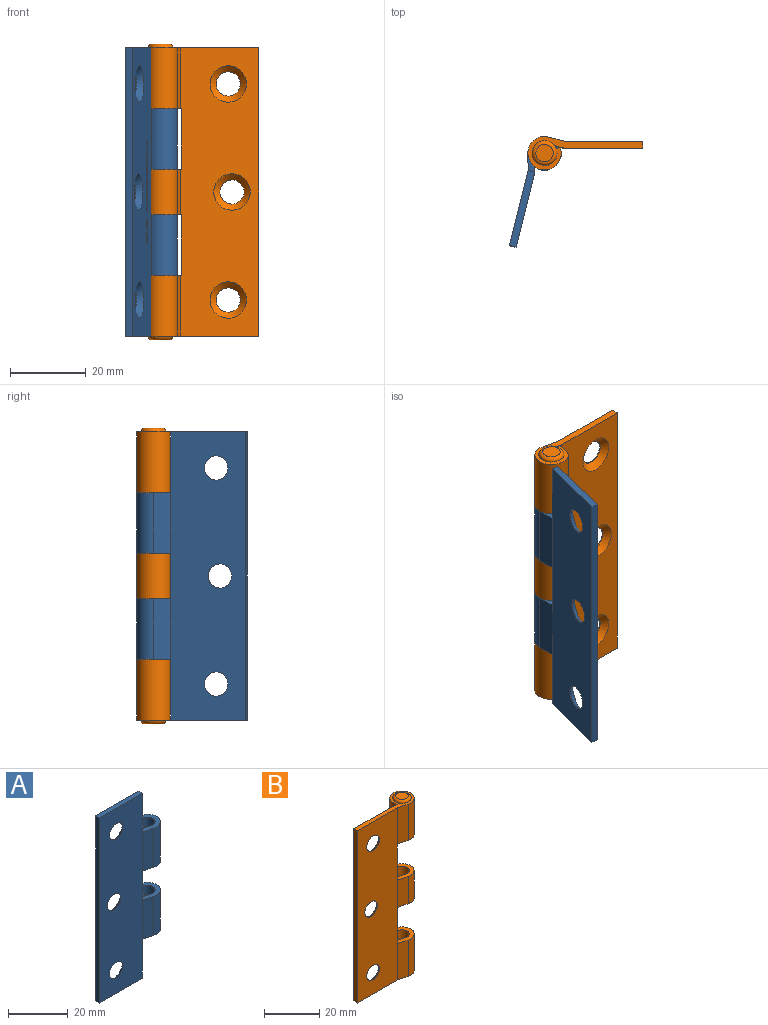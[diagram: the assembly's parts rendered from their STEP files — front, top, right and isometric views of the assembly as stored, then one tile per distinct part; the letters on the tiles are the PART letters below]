
ASSEMBLY  parts=2 mates=1
PART A: 283 faces, bbox 30.3x8.8x76 mm
  f0: cone r=3.2mm half-angle=45deg, axis (0,1,0), area 56.9mm2, adj f3,f10
  f1: cone r=3.2mm half-angle=45deg, axis (0,1,0), area 56.9mm2, adj f4,f10
  f2: cone r=3.2mm half-angle=45deg, axis (0,1,0), area 56.9mm2, adj f5,f10
  f3: cylinder r=3.2mm len=6.4mm, axis (0,1,0), area 4mm2, adj f0,f16
  f4: cylinder r=3.2mm len=6.4mm, axis (0,1,0), area 4mm2, adj f1,f16
  f5: cylinder r=3.2mm len=6.4mm, axis (0,1,0), area 4mm2, adj f2,f16
  f6: cylinder r=4.4mm len=16mm, axis (0,0,-1), area 374.3mm2, adj f17,f18,f23,f24
  f7: cylinder r=2.6mm len=16mm, axis (0,0,-1), area 221.2mm2, adj f14,f18,f23,f24
  f8: cylinder r=4.4mm len=16mm, axis (0,0,-1), area 374.3mm2, adj f12,f13,f22,f26
  f9: cylinder r=2.6mm len=16mm, axis (0,0,-1), area 221.2mm2, adj f11,f13,f22,f26
  f10: plane 76x20.64mm, normal (0,1,0), area 1324.3mm2, adj f0,f1,f2,f11,f14,f15,f19,f20
  f11: plane 16x4.54mm, normal (0.26,0.97,0), area 75.2mm2, adj f9,f10,f22,f26
  f12: plane 16x4.32mm, normal (-0.26,-0.97,0), area 71.5mm2, adj f8,f16,f22,f26
  f13: plane 16x1.69mm, normal (0.34,-0.94,0), area 28.8mm2, adj f8,f9,f22,f26
  f14: plane 16x4.54mm, normal (0.26,0.97,0), area 75.2mm2, adj f7,f10,f23,f24
  f15: plane 76x1.8mm, normal (-1,0,0), area 136.8mm2, adj f10,f16,f19,f20
  f16: plane 76x20.4mm, normal (0,-1,0), area 1453.9mm2, adj f3,f4,f5,f12,f15,f17,f19,f20
  f17: plane 16x4.32mm, normal (-0.26,-0.97,0), area 71.5mm2, adj f6,f16,f23,f24
  f18: plane 16x1.69mm, normal (0.34,-0.94,0), area 28.8mm2, adj f6,f7,f23,f24
  f19: plane 20.4x1.8mm, normal (0,0,1), area 36.7mm2, adj f10,f15,f16,f27
  f20: plane 20.4x1.8mm, normal (0,0,-1), area 36.7mm2, adj f10,f15,f16,f25
  f21: plane 12x1.8mm, normal (1,0,0), area 21.6mm2, adj f10,f16,f22,f23
  f22: plane 9.85x8.8mm, normal (0,0,-1), area 42mm2, adj f8,f9,f10,f11,f12,f13,f21
  f23: plane 9.85x8.8mm, normal (0,0,1), area 42mm2, adj f6,f7,f10,f14,f17,f18,f21
  f24: plane 9.85x8.8mm, normal (0,0,-1), area 42mm2, adj f6,f7,f10,f14,f17,f18,f25
  f25: plane 16x1.8mm, normal (1,0,0), area 28.8mm2, adj f10,f16,f20,f24
  f26: plane 9.85x8.8mm, normal (0,0,1), area 42mm2, adj f8,f9,f10,f11,f12,f13,f27
  f27: plane 16x1.8mm, normal (1,0,0), area 28.8mm2, adj f10,f16,f19,f26
  f28: plane 0.25x0.23mm, normal (1,0,0), area 0.1mm2, adj f10,f29,f45,f46
  f29: plane 1.45x0.37mm, normal (0.24,0,0.97), area 0.4mm2, adj f10,f28,f30,f46
  f30: plane 0.25x0.21mm, normal (-1,0,0), area 0.1mm2, adj f10,f29,f31,f46
  f31: plane 0.83x0.25mm, normal (-0.23,0,-0.97), area 0.2mm2, adj f10,f30,f32,f46
  f32: plane 0.31x0.25mm, normal (-0.23,0,-0.97), area 0.1mm2, adj f10,f31,f33,f46
  f33: plane 0.3x0.25mm, normal (-0.19,0,0.98), area 0.1mm2, adj f10,f32,f34,f46
  f34: plane 0.85x0.25mm, normal (-0.19,0,0.98), area 0.2mm2, adj f10,f33,f35,f46
  f35: plane 0.25x0.23mm, normal (-1,0,0), area 0.1mm2, adj f10,f34,f36,f46
  f36: plane 0.84x0.25mm, normal (-0.19,0,-0.98), area 0.2mm2, adj f10,f35,f37,f46
  f37: plane 0.28x0.25mm, normal (-0.2,0,-0.98), area 0.1mm2, adj f10,f36,f38,f46
  f38: plane 0.28x0.25mm, normal (-0.23,0,0.97), area 0.1mm2, adj f10,f37,f39,f46
  f39: plane 0.84x0.25mm, normal (-0.23,0,0.97), area 0.2mm2, adj f10,f38,f40,f46
  f40: plane 0.25x0.21mm, normal (-1,0,0), area 0.1mm2, adj f10,f39,f41,f46
  f41: plane 1.45x0.35mm, normal (0.23,0,-0.97), area 0.4mm2, adj f10,f40,f42,f46
  f42: plane 0.25x0.25mm, normal (1,0,0), area 0.1mm2, adj f10,f41,f43,f46
  f43: plane 0.87x0.25mm, normal (0.2,0,0.98), area 0.2mm2, adj f10,f42,f44,f46
  f44: plane 0.25x0.25mm, normal (0.17,0,0.99), area 0.1mm2, adj f10,f43,f45,f46
  f45: plane 1.12x0.25mm, normal (0.19,0,-0.98), area 0.3mm2, adj f10,f28,f44,f46
  f46: plane 1.64x1.45mm, normal (0,1,0), area 1.1mm2, adj f28,f29,f30,f31,f32,f33,f34,f35
  f47: plane 0.25x0.23mm, normal (1,0,0), area 0.1mm2, adj f10,f48,f64,f65
  f48: plane 1.45x0.37mm, normal (0.24,0,0.97), area 0.4mm2, adj f10,f47,f49,f65
  f49: plane 0.25x0.21mm, normal (-1,0,0), area 0.1mm2, adj f10,f48,f50,f65
  f50: plane 0.83x0.25mm, normal (-0.23,0,-0.97), area 0.2mm2, adj f10,f49,f51,f65
  f51: plane 0.31x0.25mm, normal (-0.23,0,-0.97), area 0.1mm2, adj f10,f50,f52,f65
  f52: plane 0.3x0.25mm, normal (-0.19,0,0.98), area 0.1mm2, adj f10,f51,f53,f65
  f53: plane 0.85x0.25mm, normal (-0.19,0,0.98), area 0.2mm2, adj f10,f52,f54,f65
  f54: plane 0.25x0.23mm, normal (-1,0,0), area 0.1mm2, adj f10,f53,f55,f65
  f55: plane 0.84x0.25mm, normal (-0.19,0,-0.98), area 0.2mm2, adj f10,f54,f56,f65
  f56: plane 0.28x0.25mm, normal (-0.2,0,-0.98), area 0.1mm2, adj f10,f55,f57,f65
  f57: plane 0.28x0.25mm, normal (-0.23,0,0.97), area 0.1mm2, adj f10,f56,f58,f65
  f58: plane 0.84x0.25mm, normal (-0.23,0,0.97), area 0.2mm2, adj f10,f57,f59,f65
  f59: plane 0.25x0.21mm, normal (-1,0,0), area 0.1mm2, adj f10,f58,f60,f65
  f60: plane 1.45x0.35mm, normal (0.23,0,-0.97), area 0.4mm2, adj f10,f59,f61,f65
  f61: plane 0.25x0.25mm, normal (1,0,0), area 0.1mm2, adj f10,f60,f62,f65
  f62: plane 0.87x0.25mm, normal (0.2,0,0.98), area 0.2mm2, adj f10,f61,f63,f65
  f63: plane 0.25x0.25mm, normal (0.17,0,0.99), area 0.1mm2, adj f10,f62,f64,f65
  f64: plane 1.12x0.25mm, normal (0.19,0,-0.98), area 0.3mm2, adj f10,f47,f63,f65
  f65: plane 1.64x1.45mm, normal (0,1,0), area 1.1mm2, adj f47,f48,f49,f50,f51,f52,f53,f54
  f66: plane 0.25x0.23mm, normal (1,0,0), area 0.1mm2, adj f10,f67,f83,f84
  f67: plane 1.45x0.37mm, normal (0.24,0,0.97), area 0.4mm2, adj f10,f66,f68,f84
  f68: plane 0.25x0.21mm, normal (-1,0,0), area 0.1mm2, adj f10,f67,f69,f84
  f69: plane 0.83x0.25mm, normal (-0.23,0,-0.97), area 0.2mm2, adj f10,f68,f70,f84
  f70: plane 0.31x0.25mm, normal (-0.23,0,-0.97), area 0.1mm2, adj f10,f69,f71,f84
  f71: plane 0.3x0.25mm, normal (-0.19,0,0.98), area 0.1mm2, adj f10,f70,f72,f84
  f72: plane 0.85x0.25mm, normal (-0.19,0,0.98), area 0.2mm2, adj f10,f71,f73,f84
  f73: plane 0.25x0.23mm, normal (-1,0,0), area 0.1mm2, adj f10,f72,f74,f84
  f74: plane 0.84x0.25mm, normal (-0.19,0,-0.98), area 0.2mm2, adj f10,f73,f75,f84
  f75: plane 0.28x0.25mm, normal (-0.2,0,-0.98), area 0.1mm2, adj f10,f74,f76,f84
  f76: plane 0.28x0.25mm, normal (-0.23,0,0.97), area 0.1mm2, adj f10,f75,f77,f84
  f77: plane 0.84x0.25mm, normal (-0.23,0,0.97), area 0.2mm2, adj f10,f76,f78,f84
  f78: plane 0.25x0.21mm, normal (-1,0,0), area 0.1mm2, adj f10,f77,f79,f84
  f79: plane 1.45x0.35mm, normal (0.23,0,-0.97), area 0.4mm2, adj f10,f78,f80,f84
  f80: plane 0.25x0.25mm, normal (1,0,0), area 0.1mm2, adj f10,f79,f81,f84
  f81: plane 0.87x0.25mm, normal (0.2,0,0.98), area 0.2mm2, adj f10,f80,f82,f84
  f82: plane 0.25x0.25mm, normal (0.17,0,0.99), area 0.1mm2, adj f10,f81,f83,f84
  f83: plane 1.12x0.25mm, normal (0.19,0,-0.98), area 0.3mm2, adj f10,f66,f82,f84
  f84: plane 1.64x1.45mm, normal (0,1,0), area 1.1mm2, adj f66,f67,f68,f69,f70,f71,f72,f73
  f85: plane 0.25x0.21mm, normal (1,0,0), area 0.1mm2, adj f10,f86,f88,f89
  f86: plane 0.29x0.25mm, normal (0,0,1), area 0.1mm2, adj f10,f85,f87,f89
  f87: plane 0.25x0.21mm, normal (-1,0,0), area 0.1mm2, adj f10,f86,f88,f89
  f88: plane 0.29x0.25mm, normal (0,0,-1), area 0.1mm2, adj f10,f85,f87,f89
  f89: plane 0.29x0.21mm, normal (0,1,0), area 0.1mm2, adj f85,f86,f87,f88
  f90: extruded ~0.36x0.3mm, area 0.1mm2, adj f10,f91,f99,f100
  f91: plane 0.25x0.21mm, normal (-0.99,0,-0.12), area 0.1mm2, adj f10,f90,f92,f100
  f92: extruded ~0.55x0.5mm, area 0.2mm2, adj f10,f91,f93,f100
  f93: extruded ~0.75x0.54mm, area 0.3mm2, adj f10,f92,f94,f100
  f94: extruded ~0.75x0.54mm, area 0.3mm2, adj f10,f93,f95,f100
  f95: extruded ~0.47x0.47mm, area 0.2mm2, adj f10,f94,f96,f100
  f96: plane 0.25x0.21mm, normal (0.99,0,-0.12), area 0.1mm2, adj f10,f95,f97,f100
  f97: extruded ~0.29x0.26mm, area 0.1mm2, adj f10,f96,f98,f100
  f98: extruded ~0.54x0.33mm, area 0.2mm2, adj f10,f97,f99,f100
  f99: extruded ~0.55x0.33mm, area 0.2mm2, adj f10,f90,f98,f100
  f100: plane 1.51x1.04mm, normal (0,1,0), area 0.6mm2, adj f90,f91,f92,f93,f94,f95,f96,f97
  f101: extruded ~0.75x0.56mm, area 0.3mm2, adj f10,f102,f104,f105
  f102: extruded ~0.75x0.56mm, area 0.3mm2, adj f10,f101,f103,f105
  f103: extruded ~0.74x0.56mm, area 0.3mm2, adj f10,f102,f104,f105
  f104: extruded ~0.77x0.56mm, area 0.3mm2, adj f10,f101,f103,f105
  f105: plane 1.51x1.12mm, normal (0,1,0), area 0.7mm2, adj f101,f102,f103,f104,f106,f107,f108,f109
  f106: extruded ~0.54x0.35mm, area 0.2mm2, adj f105,f107,f109,f110
  f107: extruded ~0.54x0.36mm, area 0.2mm2, adj f105,f106,f108,f110
  f108: extruded ~0.55x0.35mm, area 0.2mm2, adj f105,f107,f109,f110
  f109: extruded ~0.55x0.36mm, area 0.2mm2, adj f105,f106,f108,f110
  f110: plane 1.09x0.7mm, normal (0,1,0), area 0.6mm2, adj f106,f107,f108,f109
  f111: plane 0.25x0.21mm, normal (1,0,0), area 0.1mm2, adj f10,f112,f129,f130
  f112: plane 1.45x0.25mm, normal (0,0,1), area 0.4mm2, adj f10,f111,f113,f130
  f113: plane 0.25x0.18mm, normal (-1,0,0), area 0mm2, adj f10,f112,f114,f130
  f114: plane 0.25x0.21mm, normal (0,0,-1), area 0.1mm2, adj f10,f113,f115,f130
  f115: extruded ~0.36x0.25mm, area 0.1mm2, adj f10,f114,f116,f130
  f116: extruded ~0.34x0.25mm, area 0.1mm2, adj f10,f115,f117,f130
  f117: extruded ~0.37x0.25mm, area 0.1mm2, adj f10,f116,f118,f130
  f118: extruded ~0.49x0.37mm, area 0.2mm2, adj f10,f117,f119,f130
  f119: plane 0.99x0.25mm, normal (0,0,-1), area 0.2mm2, adj f10,f118,f120,f130
  f120: plane 0.25x0.21mm, normal (1,0,0), area 0.1mm2, adj f10,f119,f121,f130
  f121: plane 0.92x0.25mm, normal (0,0,1), area 0.2mm2, adj f10,f120,f122,f130
  f122: extruded ~0.36x0.25mm, area 0.1mm2, adj f10,f121,f123,f130
  f123: extruded ~0.43x0.29mm, area 0.1mm2, adj f10,f122,f124,f130
  f124: plane 0.84x0.25mm, normal (0,0,-1), area 0.2mm2, adj f10,f123,f125,f130
  f125: plane 0.25x0.21mm, normal (1,0,0), area 0.1mm2, adj f10,f124,f126,f130
  f126: plane 0.94x0.25mm, normal (0,0,1), area 0.2mm2, adj f10,f125,f127,f130
  f127: extruded ~0.33x0.25mm, area 0.1mm2, adj f10,f126,f128,f130
  f128: extruded ~0.52x0.29mm, area 0.2mm2, adj f10,f127,f129,f130
  f129: plane 0.75x0.25mm, normal (0,0,-1), area 0.2mm2, adj f10,f111,f128,f130
  f130: plane 1.61x1.48mm, normal (0,1,0), area 1.1mm2, adj f111,f112,f113,f114,f115,f116,f117,f118
  f131: extruded ~0.25x0.2mm, area 0.1mm2, adj f10,f132,f145,f146
  f132: extruded ~0.44x0.25mm, area 0.1mm2, adj f10,f131,f133,f146
  f133: extruded ~0.41x0.41mm, area 0.2mm2, adj f10,f132,f134,f146
  f134: extruded ~0.48x0.45mm, area 0.2mm2, adj f10,f133,f135,f146
  f135: extruded ~0.37x0.25mm, area 0.1mm2, adj f10,f134,f136,f146
  f136: plane 0.25x0.06mm, normal (0,0,1), area 0mm2, adj f10,f135,f137,f146
  f137: extruded ~0.25x0.2mm, area 0.1mm2, adj f10,f136,f138,f146
  f138: extruded ~0.25x0.24mm, area 0.1mm2, adj f10,f137,f139,f146
  f139: extruded ~0.33x0.26mm, area 0.1mm2, adj f10,f138,f140,f146
  f140: plane 0.25x0.21mm, normal (0.99,0,0.12), area 0.1mm2, adj f10,f139,f141,f146
  f141: extruded ~0.56x0.44mm, area 0.2mm2, adj f10,f140,f142,f146
  f142: extruded ~0.55x0.48mm, area 0.2mm2, adj f10,f141,f143,f146
  f143: plane 0.33x0.25mm, normal (0,0,-1), area 0.1mm2, adj f10,f142,f144,f146
  f144: extruded ~0.61x0.25mm, area 0.2mm2, adj f10,f143,f145,f146
  f145: plane 0.25x0.21mm, normal (1,0,0), area 0.1mm2, adj f10,f131,f144,f146
  f146: plane 1.51x1.12mm, normal (0,1,0), area 0.9mm2, adj f131,f132,f133,f134,f135,f136,f137,f138
  f147: plane 0.25x0.09mm, normal (0,0,1), area 0mm2, adj f146,f148,f151,f152
  f148: extruded ~0.46x0.39mm, area 0.2mm2, adj f146,f147,f149,f152
  f149: extruded ~0.26x0.25mm, area 0.1mm2, adj f146,f148,f150,f152
  f150: extruded ~0.3x0.25mm, area 0.1mm2, adj f146,f149,f151,f152
  f151: extruded ~0.35x0.25mm, area 0.1mm2, adj f146,f147,f150,f152
  f152: plane 0.65x0.55mm, normal (0,1,0), area 0.2mm2, adj f147,f148,f149,f150,f151
  f153: extruded ~0.36x0.3mm, area 0.1mm2, adj f10,f154,f162,f163
  f154: plane 0.25x0.21mm, normal (-0.99,0,-0.12), area 0.1mm2, adj f10,f153,f155,f163
  f155: extruded ~0.55x0.5mm, area 0.2mm2, adj f10,f154,f156,f163
  f156: extruded ~0.75x0.54mm, area 0.3mm2, adj f10,f155,f157,f163
  f157: extruded ~0.75x0.54mm, area 0.3mm2, adj f10,f156,f158,f163
  f158: extruded ~0.47x0.47mm, area 0.2mm2, adj f10,f157,f159,f163
  f159: plane 0.25x0.21mm, normal (0.99,0,-0.12), area 0.1mm2, adj f10,f158,f160,f163
  f160: extruded ~0.29x0.26mm, area 0.1mm2, adj f10,f159,f161,f163
  f161: extruded ~0.54x0.33mm, area 0.2mm2, adj f10,f160,f162,f163
  f162: extruded ~0.55x0.33mm, area 0.2mm2, adj f10,f153,f161,f163
  f163: plane 1.51x1.04mm, normal (0,1,0), area 0.6mm2, adj f153,f154,f155,f156,f157,f158,f159,f160
  f164: plane 0.25x0.21mm, normal (1,0,0), area 0.1mm2, adj f10,f165,f167,f168
  f165: plane 0.29x0.25mm, normal (0,0,1), area 0.1mm2, adj f10,f164,f166,f168
  f166: plane 0.25x0.21mm, normal (-1,0,0), area 0.1mm2, adj f10,f165,f167,f168
  f167: plane 0.29x0.25mm, normal (0,0,-1), area 0.1mm2, adj f10,f164,f166,f168
  f168: plane 0.29x0.21mm, normal (0,1,0), area 0.1mm2, adj f164,f165,f166,f167
  f169: extruded ~0.36x0.3mm, area 0.1mm2, adj f10,f170,f178,f179
  f170: plane 0.25x0.21mm, normal (-0.99,0,-0.12), area 0.1mm2, adj f10,f169,f171,f179
  f171: extruded ~0.55x0.5mm, area 0.2mm2, adj f10,f170,f172,f179
  f172: extruded ~0.75x0.54mm, area 0.3mm2, adj f10,f171,f173,f179
  f173: extruded ~0.75x0.54mm, area 0.3mm2, adj f10,f172,f174,f179
  f174: extruded ~0.47x0.47mm, area 0.2mm2, adj f10,f173,f175,f179
  f175: plane 0.25x0.21mm, normal (0.99,0,-0.12), area 0.1mm2, adj f10,f174,f176,f179
  f176: extruded ~0.29x0.26mm, area 0.1mm2, adj f10,f175,f177,f179
  f177: extruded ~0.54x0.33mm, area 0.2mm2, adj f10,f176,f178,f179
  f178: extruded ~0.55x0.33mm, area 0.2mm2, adj f10,f169,f177,f179
  f179: plane 1.51x1.04mm, normal (0,1,0), area 0.6mm2, adj f169,f170,f171,f172,f173,f174,f175,f176
  f180: extruded ~0.75x0.56mm, area 0.3mm2, adj f10,f181,f183,f184
  f181: extruded ~0.75x0.56mm, area 0.3mm2, adj f10,f180,f182,f184
  f182: extruded ~0.74x0.56mm, area 0.3mm2, adj f10,f181,f183,f184
  f183: extruded ~0.77x0.56mm, area 0.3mm2, adj f10,f180,f182,f184
  f184: plane 1.51x1.12mm, normal (0,1,0), area 0.7mm2, adj f180,f181,f182,f183,f185,f186,f187,f188
  f185: extruded ~0.54x0.35mm, area 0.2mm2, adj f184,f186,f188,f189
  f186: extruded ~0.54x0.36mm, area 0.2mm2, adj f184,f185,f187,f189
  f187: extruded ~0.55x0.35mm, area 0.2mm2, adj f184,f186,f188,f189
  f188: extruded ~0.55x0.36mm, area 0.2mm2, adj f184,f185,f187,f189
  f189: plane 1.09x0.7mm, normal (0,1,0), area 0.6mm2, adj f185,f186,f187,f188
  f190: plane 0.25x0.21mm, normal (1,0,0), area 0.1mm2, adj f10,f191,f193,f194
  f191: plane 0.29x0.25mm, normal (0,0,1), area 0.1mm2, adj f10,f190,f192,f194
  f192: plane 0.25x0.21mm, normal (-1,0,0), area 0.1mm2, adj f10,f191,f193,f194
  f193: plane 0.29x0.25mm, normal (0,0,-1), area 0.1mm2, adj f10,f190,f192,f194
  f194: plane 0.29x0.21mm, normal (0,1,0), area 0.1mm2, adj f190,f191,f192,f193
  f195: plane 0.25x0.21mm, normal (1,0,0), area 0.1mm2, adj f10,f196,f206,f207
  f196: plane 1.45x0.25mm, normal (0,0,1), area 0.4mm2, adj f10,f195,f197,f207
  f197: plane 0.25x0.18mm, normal (-1,0,0), area 0mm2, adj f10,f196,f198,f207
  f198: plane 0.25x0.21mm, normal (0,0,-1), area 0.1mm2, adj f10,f197,f199,f207
  f199: extruded ~0.38x0.25mm, area 0.1mm2, adj f10,f198,f200,f207
  f200: extruded ~0.59x0.4mm, area 0.2mm2, adj f10,f199,f201,f207
  f201: plane 0.89x0.25mm, normal (0,0,-1), area 0.2mm2, adj f10,f200,f202,f207
  f202: plane 0.25x0.21mm, normal (1,0,0), area 0.1mm2, adj f10,f201,f203,f207
  f203: plane 0.88x0.25mm, normal (0,0,1), area 0.2mm2, adj f10,f202,f204,f207
  f204: extruded ~0.39x0.25mm, area 0.1mm2, adj f10,f203,f205,f207
  f205: extruded ~0.48x0.31mm, area 0.2mm2, adj f10,f204,f206,f207
  f206: plane 0.79x0.25mm, normal (0,0,-1), area 0.2mm2, adj f10,f195,f205,f207
  f207: plane 1.48x0.96mm, normal (0,1,0), area 0.7mm2, adj f195,f196,f197,f198,f199,f200,f201,f202
  f208: plane 1.04x0.25mm, normal (1,0,0), area 0.3mm2, adj f10,f209,f218,f219
  f209: plane 0.25x0.21mm, normal (0,0,1), area 0.1mm2, adj f10,f208,f210,f219
  f210: plane 1.04x0.74mm, normal (-0.58,0,0.81), area 0.3mm2, adj f10,f209,f211,f219
  f211: plane 0.72x0.25mm, normal (1,0,0), area 0.2mm2, adj f10,f210,f212,f219
  f212: plane 0.25x0.21mm, normal (0,0,1), area 0.1mm2, adj f10,f211,f213,f219
  f213: plane 0.99x0.25mm, normal (-1,0,0), area 0.2mm2, adj f10,f212,f214,f219
  f214: plane 0.25x0.18mm, normal (0,0,-1), area 0mm2, adj f10,f213,f215,f219
  f215: plane 0.91x0.64mm, normal (0.58,0,-0.82), area 0.3mm2, adj f10,f214,f216,f219
  f216: plane 0.25x0.17mm, normal (0.6,0,-0.8), area 0.1mm2, adj f10,f215,f217,f219
  f217: plane 0.79x0.25mm, normal (-1,0,0), area 0.2mm2, adj f10,f216,f218,f219
  f218: plane 0.25x0.21mm, normal (0,0,-1), area 0.1mm2, adj f10,f208,f217,f219
  f219: plane 1.45x1.04mm, normal (0,1,0), area 0.7mm2, adj f208,f209,f210,f211,f212,f213,f214,f215
  f220: extruded ~1.03x0.53mm, area 0.3mm2, adj f10,f221,f224,f225
  f221: extruded ~1.03x0.53mm, area 0.3mm2, adj f10,f220,f222,f225
  f222: extruded ~0.37x0.25mm, area 0.1mm2, adj f10,f221,f223,f225
  f223: extruded ~0.82x0.25mm, area 0.2mm2, adj f10,f222,f224,f225
  f224: extruded ~1.03x0.53mm, area 0.3mm2, adj f10,f220,f223,f225
  f225: plane 2.05x1.07mm, normal (0,1,0), area 0.9mm2, adj f220,f221,f222,f223,f224,f226,f227,f228
  f226: extruded ~0.82x0.32mm, area 0.2mm2, adj f225,f227,f229,f230
  f227: extruded ~0.82x0.33mm, area 0.2mm2, adj f225,f226,f228,f230
  f228: extruded ~0.82x0.32mm, area 0.2mm2, adj f225,f227,f229,f230
  f229: extruded ~0.82x0.33mm, area 0.2mm2, adj f225,f226,f228,f230
  f230: plane 1.64x0.65mm, normal (0,1,0), area 0.9mm2, adj f226,f227,f228,f229
  f231: plane 0.78x0.25mm, normal (-1,0,0), area 0.2mm2, adj f10,f232,f242,f243
  f232: plane 0.25x0.23mm, normal (0,0,-1), area 0.1mm2, adj f10,f231,f233,f243
  f233: plane 1.07x0.25mm, normal (1,0,0), area 0.3mm2, adj f10,f232,f234,f243
  f234: extruded ~0.74x0.41mm, area 0.2mm2, adj f10,f233,f235,f243
  f235: extruded ~0.73x0.45mm, area 0.2mm2, adj f10,f234,f236,f243
  f236: extruded ~0.35x0.31mm, area 0.1mm2, adj f10,f235,f237,f243
  f237: extruded ~0.42x0.32mm, area 0.1mm2, adj f10,f236,f238,f243
  f238: plane 0.25x0.21mm, normal (0.99,0,0.12), area 0.1mm2, adj f10,f237,f239,f243
  f239: extruded ~0.6x0.53mm, area 0.2mm2, adj f10,f238,f240,f243
  f240: extruded ~0.56x0.51mm, area 0.2mm2, adj f10,f239,f241,f243
  f241: extruded ~0.84x0.47mm, area 0.2mm2, adj f10,f240,f242,f243
  f242: extruded ~0.39x0.31mm, area 0.1mm2, adj f10,f231,f241,f243
  f243: plane 2.03x1.07mm, normal (0,1,0), area 0.9mm2, adj f231,f232,f233,f234,f235,f236,f237,f238
  f244: plane 2.03x0.25mm, normal (0,0,-1), area 0.5mm2, adj f10,f245,f250,f251
  f245: plane 0.25x0.21mm, normal (1,0,0), area 0.1mm2, adj f10,f244,f246,f251
  f246: plane 1.58x0.25mm, normal (0,0,1), area 0.4mm2, adj f10,f245,f247,f251
  f247: extruded ~0.42x0.31mm, area 0.1mm2, adj f10,f246,f248,f251
  f248: plane 0.25x0.23mm, normal (0,0,1), area 0.1mm2, adj f10,f247,f249,f251
  f249: extruded ~0.52x0.49mm, area 0.2mm2, adj f10,f248,f250,f251
  f250: plane 0.25x0.13mm, normal (-1,0,0), area 0mm2, adj f10,f244,f249,f251
  f251: plane 2.03x0.62mm, normal (0,1,0), area 0.5mm2, adj f244,f245,f246,f247,f248,f249,f250
  f252: plane 0.78x0.25mm, normal (-1,0,0), area 0.2mm2, adj f10,f253,f263,f264
  f253: plane 0.25x0.23mm, normal (0,0,-1), area 0.1mm2, adj f10,f252,f254,f264
  f254: plane 1.07x0.25mm, normal (1,0,0), area 0.3mm2, adj f10,f253,f255,f264
  f255: extruded ~0.74x0.41mm, area 0.2mm2, adj f10,f254,f256,f264
  f256: extruded ~0.73x0.45mm, area 0.2mm2, adj f10,f255,f257,f264
  f257: extruded ~0.35x0.31mm, area 0.1mm2, adj f10,f256,f258,f264
  f258: extruded ~0.42x0.32mm, area 0.1mm2, adj f10,f257,f259,f264
  f259: plane 0.25x0.21mm, normal (0.99,0,0.12), area 0.1mm2, adj f10,f258,f260,f264
  f260: extruded ~0.6x0.53mm, area 0.2mm2, adj f10,f259,f261,f264
  f261: extruded ~0.56x0.51mm, area 0.2mm2, adj f10,f260,f262,f264
  f262: extruded ~0.84x0.47mm, area 0.2mm2, adj f10,f261,f263,f264
  f263: extruded ~0.39x0.31mm, area 0.1mm2, adj f10,f252,f262,f264
  f264: plane 2.03x1.07mm, normal (0,1,0), area 0.9mm2, adj f252,f253,f254,f255,f256,f257,f258,f259
  f265: extruded ~0.57x0.52mm, area 0.2mm2, adj f10,f266,f281,f282
  f266: plane 0.25x0.21mm, normal (-0.99,0,0.12), area 0.1mm2, adj f10,f265,f267,f282
  f267: extruded ~0.39x0.31mm, area 0.1mm2, adj f10,f266,f268,f282
  f268: extruded ~0.42x0.34mm, area 0.1mm2, adj f10,f267,f269,f282
  f269: extruded ~0.39x0.32mm, area 0.1mm2, adj f10,f268,f270,f282
  f270: extruded ~0.25x0.14mm, area 0mm2, adj f10,f269,f271,f282
  f271: plane 0.25x0.24mm, normal (-0.11,0,0.99), area 0.1mm2, adj f10,f270,f272,f282
  f272: plane 0.25x0.03mm, normal (-1,0,-0.09), area 0mm2, adj f10,f271,f273,f282
  f273: extruded ~0.33x0.33mm, area 0.1mm2, adj f10,f272,f274,f282
  f274: extruded ~0.3x0.26mm, area 0.1mm2, adj f10,f273,f275,f282
  f275: extruded ~0.31x0.29mm, area 0.1mm2, adj f10,f274,f276,f282
  f276: plane 0.25x0.21mm, normal (0.99,0,0.12), area 0.1mm2, adj f10,f275,f277,f282
  f277: extruded ~0.49x0.49mm, area 0.2mm2, adj f10,f276,f278,f282
  f278: extruded ~0.52x0.47mm, area 0.2mm2, adj f10,f277,f279,f282
  f279: extruded ~0.41x0.25mm, area 0.1mm2, adj f10,f278,f280,f282
  f280: extruded ~0.49x0.3mm, area 0.2mm2, adj f10,f279,f281,f282
  f281: extruded ~0.63x0.55mm, area 0.2mm2, adj f10,f265,f280,f282
  f282: plane 2.05x1.07mm, normal (0,1,0), area 0.8mm2, adj f265,f266,f267,f268,f269,f270,f271,f272
PART B: 38 faces, bbox 30.3x8.8x78 mm
  f0: cone r=3.2mm half-angle=45deg, axis (0,1,0), area 56.9mm2, adj f3,f21
  f1: cone r=3.2mm half-angle=45deg, axis (0,1,0), area 56.9mm2, adj f4,f21
  f2: cone r=3.2mm half-angle=45deg, axis (0,1,0), area 56.9mm2, adj f5,f21
  f3: cylinder r=3.2mm len=6.4mm, axis (0,1,0), area 4mm2, adj f0,f23
  f4: cylinder r=3.2mm len=6.4mm, axis (0,1,0), area 4mm2, adj f1,f23
  f5: cylinder r=3.2mm len=6.4mm, axis (0,1,0), area 4mm2, adj f2,f23
  f6: torus R=2.3mm, axis (0,0,-1), area 29mm2, adj f27,f30,f31
  f7: torus R=2.3mm, axis (0,0,1), area 29mm2, adj f26,f28,f29
  f8: cylinder r=4.4mm len=16mm, axis (0,0,-1), area 374.3mm2, adj f24,f25,f27,f34
  f9: cylinder r=2.6mm len=16mm, axis (0,0,-1), area 221.2mm2, adj f20,f25,f31,f34
  f10: cylinder r=4.4mm len=16mm, axis (0,0,-1), area 374.3mm2, adj f18,f19,f26,f36
  f11: cylinder r=2.6mm len=16mm, axis (0,0,-1), area 221.2mm2, adj f17,f19,f28,f36
  f12: cylinder r=4.4mm len=12mm, axis (0,0,-1), area 280.7mm2, adj f15,f16,f33,f35
  f13: cylinder r=2.6mm len=12mm, axis (0,0,-1), area 165.9mm2, adj f14,f16,f33,f35
  f14: plane 12x4.54mm, normal (0.26,0.97,0), area 56.4mm2, adj f13,f21,f33,f35
  f15: plane 12x4.32mm, normal (-0.26,-0.97,0), area 53.6mm2, adj f12,f23,f33,f35
  f16: plane 12x1.69mm, normal (0.34,-0.94,0), area 21.6mm2, adj f12,f13,f33,f35
  f17: plane 16x4.54mm, normal (0.26,0.97,0), area 75.2mm2, adj f11,f21,f26,f28,f36
  f18: plane 16x4.32mm, normal (-0.26,-0.97,0), area 71.5mm2, adj f10,f23,f26,f36
  f19: plane 16x1.69mm, normal (0.34,-0.94,0), area 28.8mm2, adj f10,f11,f26,f28,f36
  f20: plane 16x4.54mm, normal (0.26,0.97,0), area 75.2mm2, adj f9,f21,f27,f31,f34
  f21: plane 76x20.64mm, normal (0,1,0), area 1343.6mm2, adj f0,f1,f2,f14,f17,f20,f22,f26
  f22: plane 76x1.8mm, normal (-1,0,0), area 136.8mm2, adj f21,f23,f26,f27
  f23: plane 76x20.4mm, normal (0,-1,0), area 1453.9mm2, adj f3,f4,f5,f15,f18,f22,f24,f26
  f24: plane 16x4.32mm, normal (-0.26,-0.97,0), area 71.5mm2, adj f8,f23,f27,f34
  f25: plane 16x1.69mm, normal (0.34,-0.94,0), area 28.8mm2, adj f8,f9,f27,f31,f34
  f26: plane 30.25x8.8mm, normal (0,0,1), area 66.7mm2, adj f7,f10,f17,f18,f19,f21,f22,f23
  f27: plane 30.25x8.8mm, normal (0,0,-1), area 66.7mm2, adj f6,f8,f20,f21,f22,f23,f24,f25
  f28: plane 5.71x5.2mm, normal (0,0,-1), area 22.3mm2, adj f7,f11,f17,f19
  f29: plane 4.6x4.6mm, normal (0,0,1), area 16.6mm2, adj f7
  f30: plane 4.6x4.6mm, normal (0,0,-1), area 16.6mm2, adj f6
  f31: plane 5.71x5.2mm, normal (0,0,1), area 22.3mm2, adj f6,f9,f20,f25
  f32: plane 16x1.8mm, normal (1,0,0), area 28.8mm2, adj f21,f23,f33,f34
  f33: plane 9.85x8.8mm, normal (0,0,-1), area 42mm2, adj f12,f13,f14,f15,f16,f21,f32
  f34: plane 9.85x8.8mm, normal (0,0,1), area 42mm2, adj f8,f9,f20,f21,f24,f25,f32
  f35: plane 9.85x8.8mm, normal (0,0,1), area 42mm2, adj f12,f13,f14,f15,f16,f21,f37
  f36: plane 9.85x8.8mm, normal (0,0,-1), area 42mm2, adj f10,f11,f17,f18,f19,f21,f37
  f37: plane 16x1.8mm, normal (1,0,0), area 28.8mm2, adj f21,f23,f35,f36
PLACE A rot(axis=(0.79,0.62,0),180deg) t=(0,0,0)mm
PLACE B rot(axis=(0,0,1),180deg) t=(0,0,0)mm
MATE revolute A.f6 <-> B.f6  axis (0,0,1) through (0,0,22)mm
